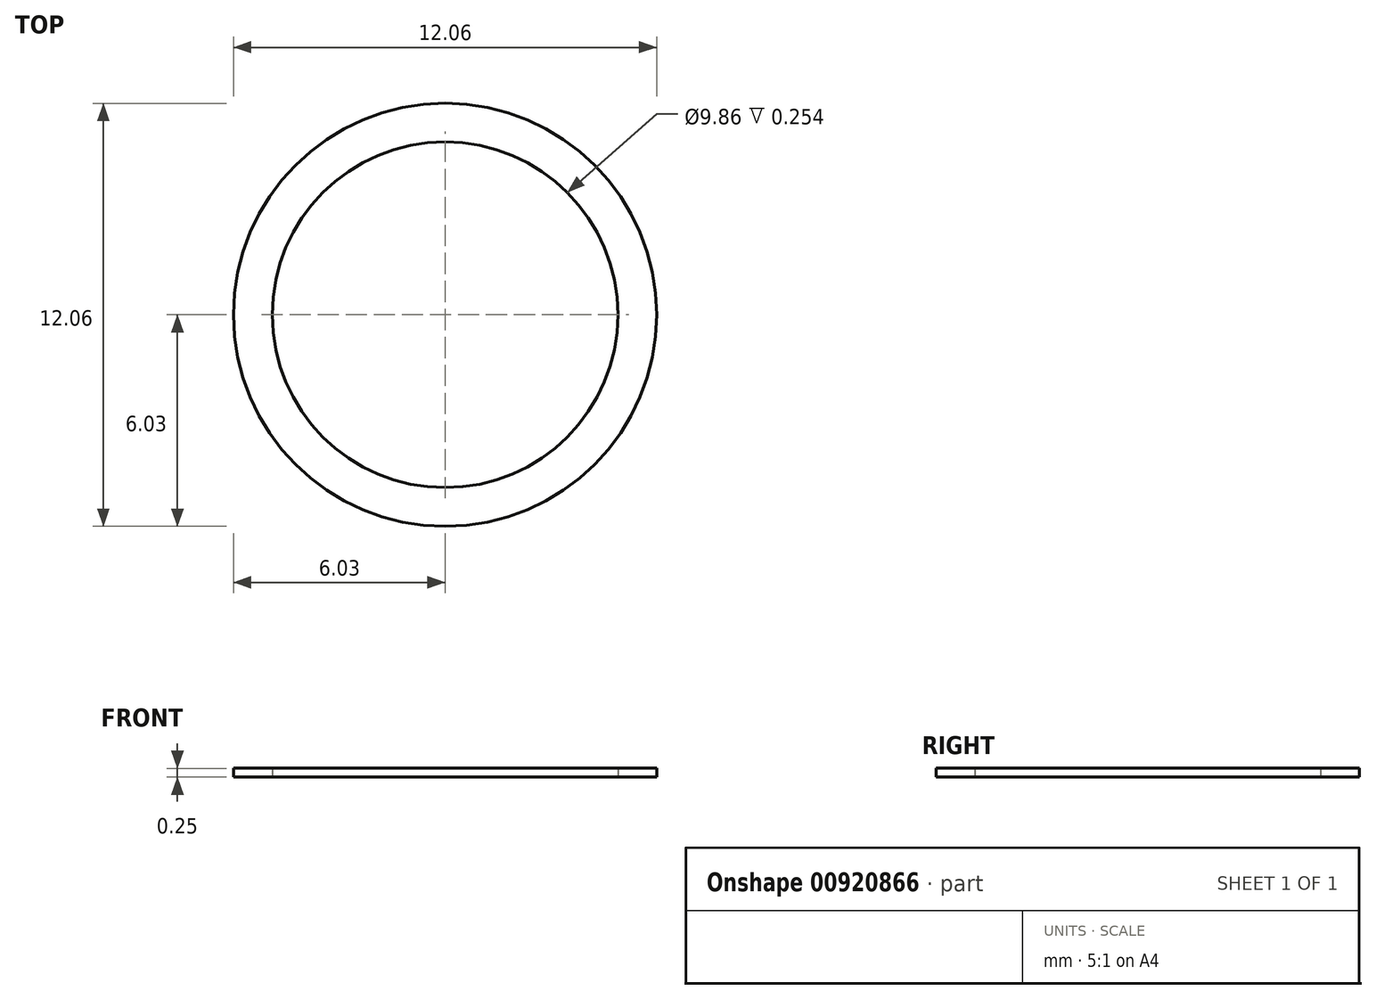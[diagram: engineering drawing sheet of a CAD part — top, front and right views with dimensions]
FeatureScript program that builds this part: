
annotation { "Feature Type Name" : "Feature", "Feature Type Description" : "" }
export const myFeature = defineFeature(function(context is Context, id is Id, definition is map)
    precondition{}
    {
        {
            var Q0;
            Q0=qCreatedBy(makeId("Top.planeOp"),FACE);
            var sketch = newSketch(context, id + "F0", { "sketchPlane" : qUnion([Q0])});
            skCircle(sketch, "E0", {"center": v(0, 0) * mm, "radius": 6.03 * mm});
            skCircle(sketch, "E1", {"center": v(0, 0) * mm, "radius": 4.93 * mm});
            skSolve(sketch);
        }
        {
            var Q0;
            Q0 = qSketchRegion(id + "F0", true);
            extrude(context, id + "F1", {"entities" : qUnion([Q0]), "depth" : 0.25 * mm, "offsetDistance" : 25.4 * mm});
        }
    });
